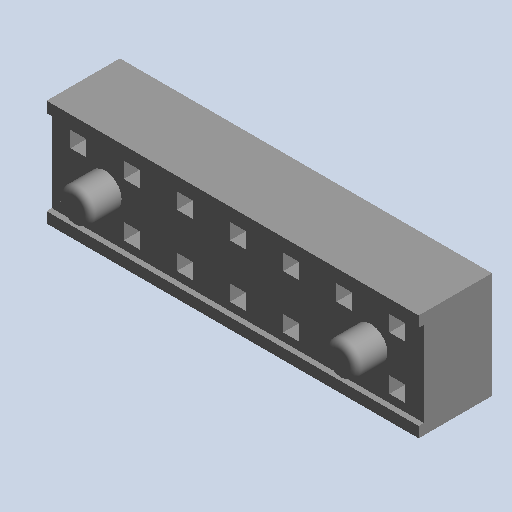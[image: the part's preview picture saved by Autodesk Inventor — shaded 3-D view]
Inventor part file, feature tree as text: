
AUTODESK INVENTOR PART (.ipt)
format: ipt  version: 2024.2 (Build 282272000, 272)  size: 216,064 bytes
history: native  units: mm (DEFAULTED — no unit token found)
features: other x14, sketch x5, extrude x3, revolve x2, pattern_linear x1
ambient origin geometry x8: Origin, YZ Plane, XZ Plane, XY Plane, X Axis, Y Axis, Z Axis, Center Point
bodies: Solid1 (feature_tree)
feature tree (25):
  extrude  "Extrusion1"  Depth=17.78mm TaperAngle=0.0deg
  extrude  "Extrusion2"  TaperAngle=360.0deg  [1 undecoded]
  revolve  "Revolution1"  [1 undecoded]
  revolve  "Revolution2"  [1 undecoded]
  extrude  "Extrusion3"  [1 undecoded]
  pattern_linear  "Rectangular Pattern1"  [2 undecoded]
  other  "socket_to_dummy_XY"
  other  "socket_to_dummy_YZ"
  other  "socket_to_dummy_ZX"
  other  "socket_to_dummy_X"
  other  "socket_to_dummy_Y"
  other  "socket_to_dummy_Z"
  other  "socket_to_dummy_Center"
  other  "socket_to_pad_XY"
  other  "socket_to_pad_YZ"
  other  "socket_to_pad_ZX"
  other  "socket_to_pad_X"
  other  "socket_to_pad_Y"
  other  "socket_to_pad_Z"
  other  "socket_to_pad_Center"
  sketch  "Sketch_1"  dims[d0=3.5052mm d1=0.0mm d2=17.78mm d3=0.0mm]
  sketch  "Sketch_4"  dims[d4=360.0deg d5=360.0deg]
  sketch  "Sketch_9"  dims[d6=1.27mm d7=0.0mm d8=60.0mm d10=2.54mm d11=10.0mm d13=0.0mm]
  sketch  "Sketch_10"  dims[d14=0.0mm]
  sketch  "Sketch_11"
note: 6 required parameter values undecoded (feature->parameter linkage not recoverable at this tier; creation-order binding heuristic only, values carry confidence <= 0.55)